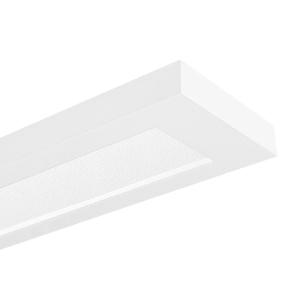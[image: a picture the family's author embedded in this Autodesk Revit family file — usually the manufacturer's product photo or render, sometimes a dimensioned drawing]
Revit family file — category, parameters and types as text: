
# Revit family: 3f_filippi_-_3f_travetta_di_lgs_3f_filippi_-_11603_-_3f_travetta_led_di_2x30w-940_lgs_l1590
name_source: partatom
category: Lighting Fixtures
units: mm (PartAtom-declared; Revit-internal decimal feet)

## family parameters
Cut with Voids When Loaded = No
Host = Face
Light Source = No
Part Type = Normal
Room Calculation Point = No
Round Connector Dimension = Use Diameter
Shared = No

## types (1)
- 3F Filippi - 3F Travetta DI LGS (1 x LED, 4963 lm, 66 W, 4000 K)
    Apparent Load = 66 VA
    Approval mark = ENEC
    CIE Flux Codes = 64 93 99 85 100
    Color Rendering = 90
    Color Temperature = 4000 K
    Control Gear = Electronic ballast
    Default Elevation = 1800 mm
    Description = ILLUMINOTECHNICAL
Luminous efficiency 100% (DLOR 85%, ULOR 15%).
Initial luminous flux of the luminaire 4963 lm.
Symmetric direct-indirect distribution.
Installation Interdistance Transv.D = 1.18 x hu - Long.D = 1.18 x hu.
Average luminance <3000 cd/m² for radial angles >65°.
Tabular UGR (CIE 117 - 4H-8H; S=0.25H; 70/50/20): RUG 17.2 - 17.7.
Beam angle: 89° - 91°.
Luminous efficacy 75 lm/W.
Lifetime (L93/B10): 30000 h. (tq+25°C)
Lifetime (L90/B10): 50000 h. (tq+25°C)
Lifetime (L85/B10): 80000 h. (tq+25°C)
Lifetime (L80/B10): 100000 h. (tq+25°C)
Sudden decreased luminous flux after 50000 hours: 0% (C0).
Photobiological safety in compliance with IEC/TR 62778: RG0 risk exempt, (IEC 62471).
In compliance with IEC/EN 62722-2-1 - IEC/EN 62717 standards.

SOURCE
2 linear LED modules 30W/940.
Energy efficiency class (UE 2019/2020 - UE 2019/2015): E.
CIE 13.3 Colour rendering index: CRI >90 (R9 >50%).
IES TM-30 Fidelity Index: Rf = 92 Rg = 101.
CCT nominal colour temperature 4000 K.
Colour initial tolerance (MacAdam): SDCM 2.

MECHANICAL
Housing with squared shape in white painted galvannealed steel, with nonreflecting surface.
Flow recuperator in semi-glossy aluminium.
LGS micro-prismatic flat diffuser in transparent methacrylate (PMMA), multi-lenticular exterior, anti-glare.
Anti-glare opal polycarbonate filter for brightness uniformity.
Upper holes closing film made of opal polycarbonate.
Luminaire with limited surface temperature. - D - (EN 60598-2-24)
Dimensions: 1590x190 mm, height 60 mm. Weight 5.6 kg.
IP20 protection degree.
Glow-wire test resistance 650°C.

ELECTRICAL
Halogen Free electronic wiring 230V-50/60Hz, power factor 0.95, THD <25%, constant output current, SELV, class I, 1 driver.
Power of the luminaire 66 W.
CE - IEC 60598-1 - EN 60598-1.
SAFE FLICKER: PstLM=<1 and SVM=<0.4 (IEC TR 61547-1 and IEC TR 63158), to ensure a more comfortable and safe light.
Luminaire compliant with EN 60598-2-22 for power supply from a centralised emergency system CPSS (Central Power Supply System), not incorporated in the luminaire - high risk areas excluded. The default power and flux are 100% in AC and 100% in DC.
Ambient temperature from 0°C to +25°C.
Temperature class T6 max 85°C.
Relative humidity UR: <85%.

INSTALLATION
Suspended.
All accessories dedicated to this product are available on the Catalog and on our website www.3F-Filippi.com.

APPLICATIONS
In environments, even with reduced height, requiring a comfortable light.
In environments with VDTs, managerial offices and staterooms, public offices and schools.

WARNING
Luminaire designed for disposal/recycling at end-of-life.
Replaceable (LED only) light source by a professional. Replaceable control gear by a professional.
    Height = 60 mm  [stored 0.19685 ft]
    Lamp = 1 x LED
    Lamp Light Flux = 4963 lm
    Lamp Power = 66 W
    Lamp count = 1
    Length = 1590 mm
    Lifetime = 50000 h
    Luminous efficacy = 75 lm/W
    Manufacturer = 3F Filippi
    ModVariant = No
    Model = 3F Filippi - 11603 - 3F Travetta LED DI 2x30W-940 LGS L1590
    Mounting Place = Ceiling
    Mounting Type = Pendant
    Number of Poles = 1
    OnlyDefault = Yes
    Power Factor = 1
    Product Name = 3F Filippi - 3F Travetta DI LGS
    Product group = pendant luminaire
    ProductGroupID = 9
    Protection Class = Protection class I
    Protection Degree = IP 20
    RLX_Detail_Level = 1
    RLX_Emergency_Light_Flux = 0 lm
    RLX_Emergency_Type = 0
    RLX_Emergency_Type_DB = No
    RlxData = <blob elided: 50493 chars, md5=c6cb76c4>
    Socket = socket
    Standby Power = 0 W
    System Light Flux = 4963 lm
    System Power = 66 W
    Type Comments = Product without accessories
    Type Image = 3ffilippi_3f_travetta_led_lgs.jpg
    URL = http://relux.com
    VarID = ---
    Voltage = 0 V
    Weight = 0.00 kg
    Width = 190 mm  [stored 0.62336 ft]

note: [stored X ft] marks values corroborated as IEEE doubles in the binary element streams (Revit-internal decimal feet)

## geometry (parser evidence)
native form markers: Blend x4, Sweep x11
no freeform markers — native parametric forms only
